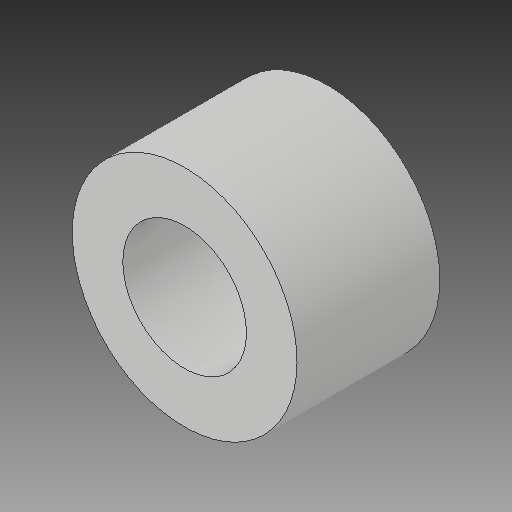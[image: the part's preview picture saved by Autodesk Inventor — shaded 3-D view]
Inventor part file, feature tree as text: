
AUTODESK INVENTOR PART (.ipt)
format: ipt  version: 2018 (Build 220112000, 112)  size: 102,400 bytes
history: native  units: mm
features: other x3, sketch x1
ambient origin geometry x8: Origin, YZ Plane, XZ Plane, XY Plane, X Axis, Y Axis, Z Axis, Center Point
bodies: Solid1 (feature_tree)
feature tree (4):
  other  "Small-Aluminium-Spacer.ipt"
  other  "Solid1::Small-Aluminium-Spacer.ipt"
  other  "TaggingFeature1"
  sketch  "Sketch1"  dims[d0=10.0mm]
